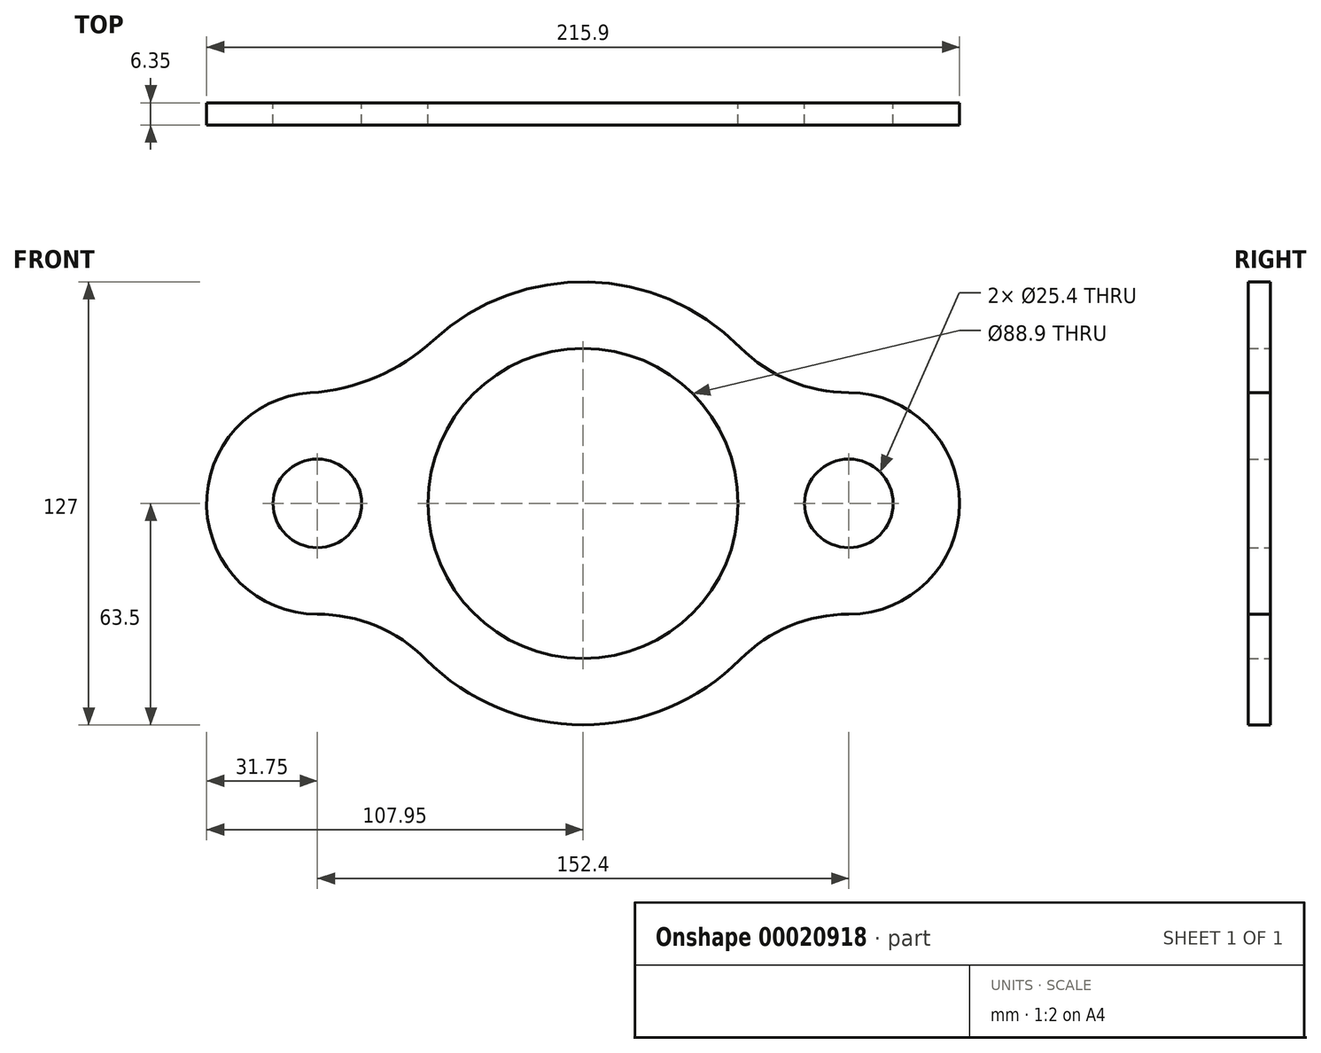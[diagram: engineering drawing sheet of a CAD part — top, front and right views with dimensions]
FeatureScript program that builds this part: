
annotation { "Feature Type Name" : "Feature", "Feature Type Description" : "" }
export const myFeature = defineFeature(function(context is Context, id is Id, definition is map)
    precondition{}
    {
        {
            var Q0;
            Q0=qCreatedBy(makeId("Front.planeOp"),FACE);
            var sketch = newSketch(context, id + "F0", { "sketchPlane" : qUnion([Q0])});
            skCircle(sketch, "E0", {"center": v(0, 0) * mm, "radius": 44.45 * mm});
            skCircle(sketch, "E1", {"center": v(-76.2, 0) * mm, "radius": 12.7 * mm});
            skCircle(sketch, "E2", {"center": v(76.2, 0) * mm, "radius": 12.7 * mm});
            skCircle(sketch, "E3", {"center": v(0, 0) * mm, "radius": 63.5 * mm});
            skCircle(sketch, "E4", {"center": v(-76.2, 0) * mm, "radius": 31.75 * mm});
            skCircle(sketch, "E5", {"center": v(76.2, 0) * mm, "radius": 31.75 * mm});
            skArc(sketch, "E6", {"start": v(-78.27, 31.68) * mm, "mid": v(-59.31, 36.21) * mm, "end": v(-42.94, 46.78) * mm});
            skArc(sketch, "E7", {"start": v(-45.09, -44.71) * mm, "mid": v(-59.35, -35.12) * mm, "end": v(-76.2, -31.75) * mm});
            skArc(sketch, "E8", {"start": v(45.09, 44.71) * mm, "mid": v(59.35, 35.12) * mm, "end": v(76.2, 31.75) * mm});
            skArc(sketch, "E9", {"start": v(76.2, -31.75) * mm, "mid": v(59.35, -35.12) * mm, "end": v(45.09, -44.71) * mm});
            skSolve(sketch);
        }
        {
            var Q0;
            {var subQ3=sQuery(id+"F0.wireOp",EDGE,"E0");var subQ6=sQuery(id+"F0.wireOp",EDGE,"E4");var subQ8=makeQuery(id+"F0.imprint","INTERSECT",VERTEX,{"derivedFrom":[subQ3,subQ6]});Q0=makeQuery(id+"F0.imprint","IMPRINT",FACE,{"disambiguationData":[TD([[makeQuery(id+"F0.imprint","IMPRINT",EDGE,{"disambiguationData":[TD([[subQ8,-1.0]])],"derivedFrom":subQ3}),-1.0]])]});}
            var Q1;
            {var subQ5=sQuery(id+"F0.wireOp",EDGE,"E1");Q1=makeQuery(id+"F0.imprint","IMPRINT",FACE,{"disambiguationData":[TD([[makeQuery(id+"F0.imprint","IMPRINT",EDGE,{"derivedFrom":subQ5}),-1.0]])]});}
            var Q2;
            {var subQ1=sQuery(id+"F0.wireOp",EDGE,"E3");var subQ5=makeQuery(id+"F0.imprint","INTERSECT",VERTEX,{"derivedFrom":[sQuery(id+"F0.wireOp",EDGE,"E1"),subQ1]});Q2=makeQuery(id+"F0.imprint","IMPRINT",FACE,{"disambiguationData":[TD([[makeQuery(id+"F0.imprint","IMPRINT",EDGE,{"disambiguationData":[TD([[subQ5,1.0]])],"derivedFrom":subQ1}),1.0]])]});}
            var Q3;
            {var subQ3=sQuery(id+"F0.wireOp",EDGE,"E0");var subQ5=sQuery(id+"F0.wireOp",EDGE,"E4");var subQ7=makeQuery(id+"F0.imprint","INTERSECT",VERTEX,{"derivedFrom":[subQ3,subQ5]});Q3=makeQuery(id+"F0.imprint","IMPRINT",FACE,{"disambiguationData":[TD([[makeQuery(id+"F0.imprint","IMPRINT",EDGE,{"disambiguationData":[TD([[subQ7,1.0]])],"derivedFrom":subQ3}),-1.0]])]});}
            var Q4;
            {var subQ0=sQuery(id+"F0.wireOp",EDGE,"E6");Q4=makeQuery(id+"F0.imprint","IMPRINT",FACE,{"disambiguationData":[TD([[makeQuery(id+"F0.imprint","IMPRINT",EDGE,{"derivedFrom":subQ0}),-1.0]])]});}
            var Q5;
            {var subQ1=sQuery(id+"F0.wireOp",EDGE,"E3");var subQ5=makeQuery(id+"F0.imprint","INTERSECT",VERTEX,{"derivedFrom":[sQuery(id+"F0.wireOp",EDGE,"E2"),subQ1]});Q5=makeQuery(id+"F0.imprint","IMPRINT",FACE,{"disambiguationData":[TD([[makeQuery(id+"F0.imprint","IMPRINT",EDGE,{"disambiguationData":[TD([[subQ5,-1.0]])],"derivedFrom":subQ1}),1.0]])]});}
            var Q6;
            {var subQ5=sQuery(id+"F0.wireOp",EDGE,"E2");Q6=makeQuery(id+"F0.imprint","IMPRINT",FACE,{"disambiguationData":[TD([[makeQuery(id+"F0.imprint","IMPRINT",EDGE,{"derivedFrom":subQ5}),-1.0]])]});}
            var Q7;
            {var subQ0=sQuery(id+"F0.wireOp",EDGE,"E8");Q7=makeQuery(id+"F0.imprint","IMPRINT",FACE,{"disambiguationData":[TD([[makeQuery(id+"F0.imprint","IMPRINT",EDGE,{"derivedFrom":subQ0}),-1.0]])]});}
            var Q8;
            {var subQ0=sQuery(id+"F0.wireOp",EDGE,"E9");Q8=makeQuery(id+"F0.imprint","IMPRINT",FACE,{"disambiguationData":[TD([[makeQuery(id+"F0.imprint","IMPRINT",EDGE,{"derivedFrom":subQ0}),-1.0]])]});}
            var Q9;
            {var subQ0=sQuery(id+"F0.wireOp",EDGE,"E7");Q9=makeQuery(id+"F0.imprint","IMPRINT",FACE,{"disambiguationData":[TD([[makeQuery(id+"F0.imprint","IMPRINT",EDGE,{"derivedFrom":subQ0}),-1.0]])]});}
            extrude(context, id + "F1", {"entities" : qUnion([Q0, Q1, Q2, Q3, Q4, Q5, Q6, Q7, Q8, Q9]), "depth" : 6.35 * mm});
        }
    });
